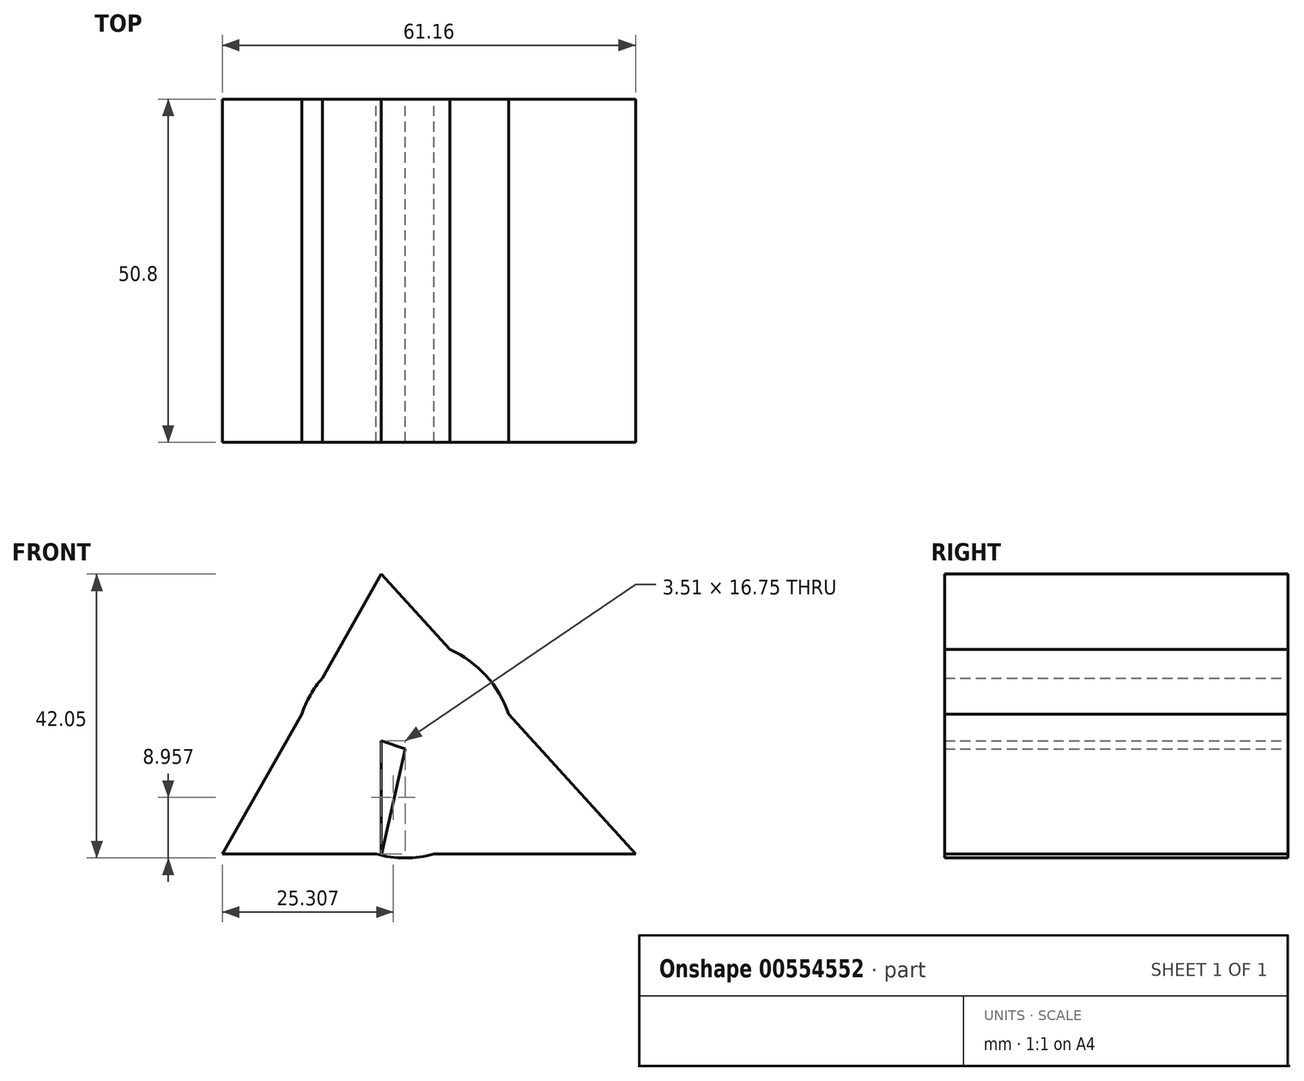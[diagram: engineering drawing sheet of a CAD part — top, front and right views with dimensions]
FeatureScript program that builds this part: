
annotation { "Feature Type Name" : "Feature", "Feature Type Description" : "" }
export const myFeature = defineFeature(function(context is Context, id is Id, definition is map)
    precondition{}
    {
        {
            var Q0;
            Q0=qCreatedBy(makeId("Front.planeOp"),FACE);
            var sketch = newSketch(context, id + "F0", { "sketchPlane" : qUnion([Q0])});
            skLineSegment(sketch, "E0", {"start": v(0, 41.66) * mm, "end": v(0, 0) * mm});
            skLineSegment(sketch, "E1", {"start": v(-23.55, 0.2) * mm, "end": v(0, 41.66) * mm});
            skLineSegment(sketch, "E2", {"start": v(0, 41.66) * mm, "end": v(37.61, 0.2) * mm});
            skLineSegment(sketch, "E3", {"start": v(-23.55, 0.2) * mm, "end": v(37.61, 0.2) * mm});
            skCircle(sketch, "E4", {"center": v(3.51, 15.75) * mm, "radius": 16.14 * mm});
            skPoint(sketch, "E4.first.point", {"position": v(0, 0) * mm});
            skPoint(sketch, "E4.second.point", {"position": v(18.8, 20.92) * mm});
            skPoint(sketch, "E4.third.point", {"position": v(-11.78, 20.92) * mm});
            skLineSegment(sketch, "E5", {"start": v(18.8, 20.92) * mm, "end": v(3.51, 15.75) * mm});
            skLineSegment(sketch, "E6", {"start": v(3.51, 15.75) * mm, "end": v(-11.78, 20.92) * mm});
            skLineSegment(sketch, "E7", {"start": v(3.51, 15.75) * mm, "end": v(0, 0) * mm});
            skSolve(sketch);
        }
        {
            var Q0;
            Q0 = qSketchRegion(id + "F0", true);
            extrude(context, id + "F1", {"entities" : qUnion([Q0]), "depth" : 50.8 * mm, "offsetDistance" : 25.4 * mm, "symmetric" : true});
        }
    });
